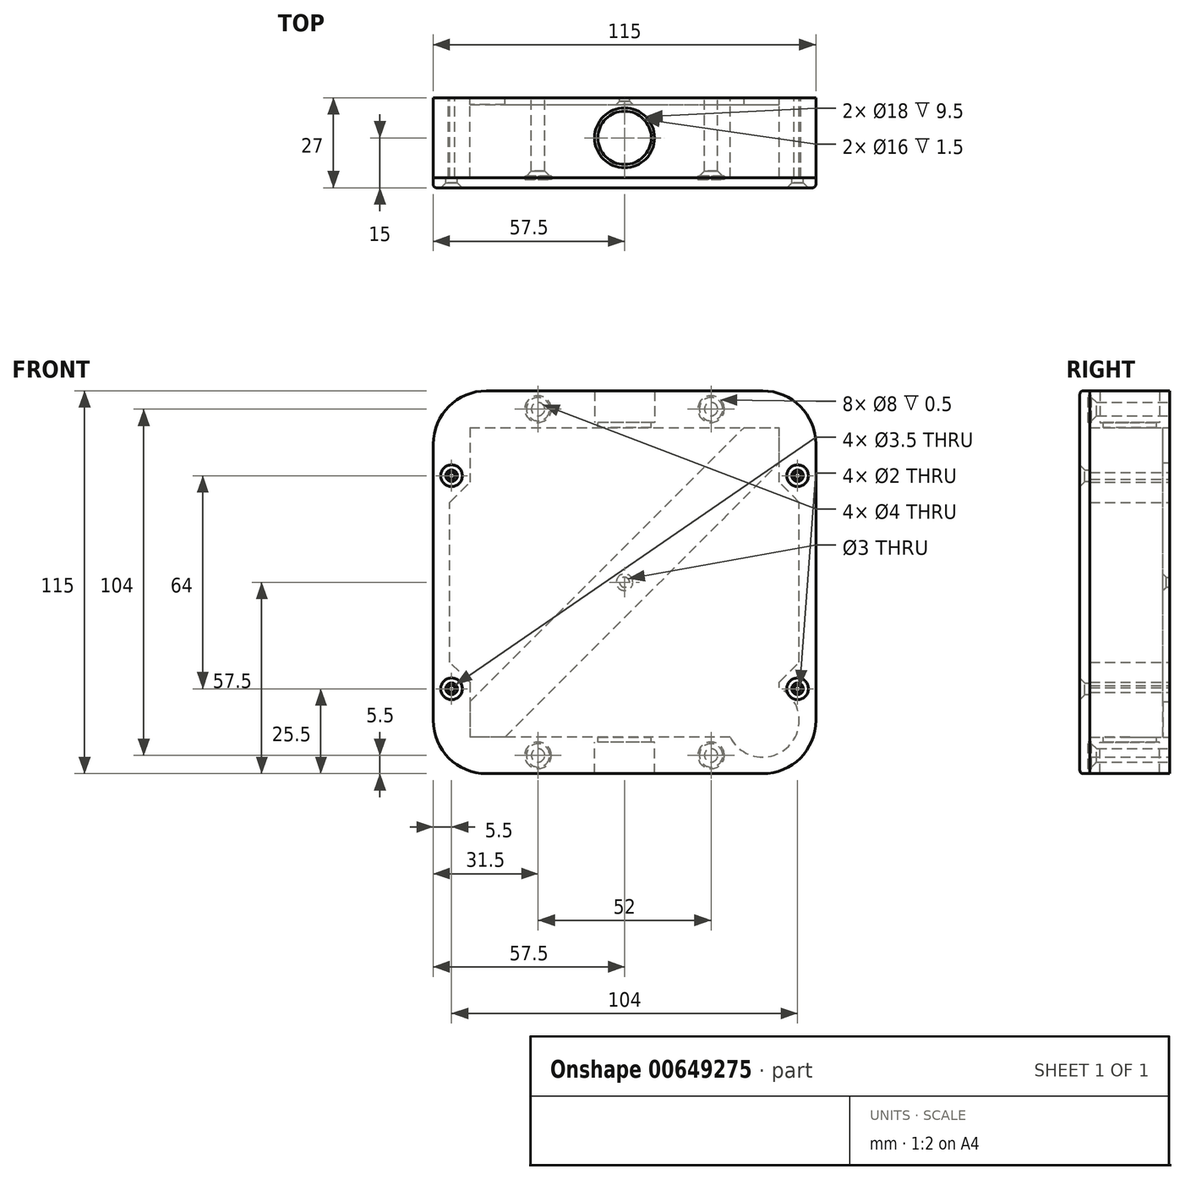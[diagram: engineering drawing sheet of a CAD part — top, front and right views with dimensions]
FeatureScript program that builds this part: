
annotation { "Feature Type Name" : "Feature", "Feature Type Description" : "" }
export const myFeature = defineFeature(function(context is Context, id is Id, definition is map)
    precondition{}
    {
        {
            var Q0;
            Q0=qCreatedBy(makeId("Front.planeOp"),FACE);
            var sketch = newSketch(context, id + "F0", { "sketchPlane" : qUnion([Q0])});
            skCircle(sketch, "E0", {"center": v(-26, 122) * mm, "radius": 2 * mm});
            skCircle(sketch, "E1", {"center": v(26, 18) * mm, "radius": 2 * mm});
            skLineSegment(sketch, "E2", {"start": v(46.5, 70) * mm, "end": v(-46.5, 70) * mm});
            skLineSegment(sketch, "E3.bottom", {"start": v(-46.5, 116.5) * mm, "end": v(46.5, 116.5) * mm});
            skLineSegment(sketch, "E3.left", {"start": v(-46.5, 116.5) * mm, "end": v(-46.5, 23.5) * mm});
            skArc(sketch, "E4", {"start": v(31.7, 23.5) * mm, "mid": v(49.28, 20.72) * mm, "end": v(46.5, 38.3) * mm});
            skArc(sketch, "E5", {"start": v(41.5, 12.5) * mm, "mid": v(52.81, 17.19) * mm, "end": v(57.5, 28.5) * mm});
            skArc(sketch, "E6", {"start": v(-57.5, 28.5) * mm, "mid": v(-52.81, 17.19) * mm, "end": v(-41.5, 12.5) * mm});
            skArc(sketch, "E7", {"start": v(-41.5, 127.5) * mm, "mid": v(-52.81, 122.81) * mm, "end": v(-57.5, 111.5) * mm});
            skArc(sketch, "E8", {"start": v(41.5, 127.5) * mm, "mid": v(52.81, 122.81) * mm, "end": v(57.5, 111.5) * mm});
            skLineSegment(sketch, "E9", {"start": v(0, 70) * mm, "end": v(0, 53.27) * mm});
            skLineSegment(sketch, "E10", {"start": v(-57.5, 28.5) * mm, "end": v(-57.5, 111.5) * mm});
            skLineSegment(sketch, "E11", {"start": v(-41.5, 127.5) * mm, "end": v(41.5, 127.5) * mm});
            skLineSegment(sketch, "E12", {"start": v(57.5, 111.5) * mm, "end": v(57.5, 28.5) * mm});
            skLineSegment(sketch, "E13", {"start": v(41.5, 12.5) * mm, "end": v(-41.5, 12.5) * mm});
            skCircle(sketch, "E14", {"center": v(-26, 18) * mm, "radius": 2 * mm});
            skCircle(sketch, "E15", {"center": v(26, 122) * mm, "radius": 2 * mm});
            skLineSegment(sketch, "E16", {"start": v(46.5, 38.3) * mm, "end": v(46.5, 116.5) * mm});
            skLineSegment(sketch, "E17", {"start": v(31.7, 23.5) * mm, "end": v(-46.5, 23.5) * mm});
            skCircle(sketch, "E18", {"center": v(52, 38) * mm, "radius": 1 * mm});
            skCircle(sketch, "E19", {"center": v(-52, 102) * mm, "radius": 1 * mm});
            skCircle(sketch, "E20", {"center": v(52, 102) * mm, "radius": 1 * mm});
            skCircle(sketch, "E21", {"center": v(-52, 38) * mm, "radius": 1 * mm});
            skLineSegment(sketch, "E22", {"start": v(-35.9, 23.5) * mm, "end": v(46.5, 105.9) * mm});
            skLineSegment(sketch, "E23", {"start": v(-46.5, 34.1) * mm, "end": v(35.9, 116.5) * mm});
            skCircle(sketch, "E24", {"center": v(0, 70) * mm, "radius": 1.5 * mm});
            skLineSegment(sketch, "E25", {"start": v(-46.5, 40) * mm, "end": v(-52.5, 46) * mm});
            skLineSegment(sketch, "E26", {"start": v(-52.5, 46) * mm, "end": v(-52.5, 94) * mm});
            skLineSegment(sketch, "E27", {"start": v(-52.5, 94) * mm, "end": v(-46.5, 100) * mm});
            skLineSegment(sketch, "E28", {"start": v(46.5, 40) * mm, "end": v(52.5, 46) * mm});
            skLineSegment(sketch, "E29", {"start": v(52.5, 46) * mm, "end": v(52.5, 94) * mm});
            skLineSegment(sketch, "E30", {"start": v(52.5, 94) * mm, "end": v(46.5, 100) * mm});
            skSolve(sketch);
        }
        {
            var Q0;
            Q0=qSketchRegion(id+"F0",true);
            extrude(context, id + "F1", {"entities" : qUnion([Q0]), "depth" : 24 * mm, "offsetDistance" : 25 * mm});
        }
        {
            var Q0;
            Q0=makeQuery(id+"F1.opExtrude","CAP_EDGE",EDGE,{"disambiguationData":[OSD([sQuery(id+"F0.wireOp",EDGE,"E0")])],"isStart":false});
            var Q1;
            Q1=makeQuery(id+"F1.opExtrude","CAP_EDGE",EDGE,{"disambiguationData":[OSD([sQuery(id+"F0.wireOp",EDGE,"E1")])],"isStart":false});
            var Q2;
            Q2=makeQuery(id+"F1.opExtrude","CAP_EDGE",EDGE,{"disambiguationData":[OSD([sQuery(id+"F0.wireOp",EDGE,"E14")])],"isStart":false});
            var Q3;
            Q3=makeQuery(id+"F1.opExtrude","CAP_EDGE",EDGE,{"disambiguationData":[OSD([sQuery(id+"F0.wireOp",EDGE,"E15")])],"isStart":false});
            chamfer(context, id + "F2", {"entities" : qUnion([Q0, Q1, Q2, Q3]), "width" : 2 * mm, "tangentPropagation" : true});
        }
        {
            var Q0;
            Q0=qCreatedBy(makeId("Top.planeOp"),FACE);
            cPlane(context, id + "F3", {"entities" : qUnion([Q0]), "cplaneType" : CPlaneType.OFFSET, "offset" : 118 * mm, "width" : 150 * mm, "height" : 150 * mm});
        }
        {
            var Q0;
            Q0=qCreatedBy(id+"F3.planeOp",FACE);
            var sketch = newSketch(context, id + "F4", { "sketchPlane" : qUnion([Q0])});
            skCircle(sketch, "E31", {"center": v(0, -12) * mm, "radius": 9 * mm});
            skCircle(sketch, "E32", {"center": v(0, -12) * mm, "radius": 8 * mm});
            skSolve(sketch);
        }
        {
            var Q0;
            Q0=qSketchRegion(id+"F4",true);
            extrude(context, id + "F5", {"entities" : qUnion([Q0]), "operationType" : NewBodyOperationType.REMOVE, "oppositeDirection" : true, "depth" : -25 * mm, "offsetDistance" : 25 * mm});
        }
        {
            var Q0;
            Q0=makeQuery(id+"F4.imprint","IMPRINT",FACE,{"disambiguationData":[TD([[makeQuery(id+"F4.imprint","IMPRINT",EDGE,{"derivedFrom":sQuery(id+"F4.wireOp",EDGE,"E32")}),1.0]])]});
            extrude(context, id + "F6", {"entities" : qUnion([Q0]), "operationType" : NewBodyOperationType.REMOVE, "endBound" : BoundingType.SYMMETRIC, "oppositeDirection" : true, "depth" : 27 * mm, "offsetDistance" : 25 * mm});
        }
        {
            var Q0;
            Q0=qCreatedBy(makeId("Top.planeOp"),FACE);
            cPlane(context, id + "F7", {"entities" : qUnion([Q0]), "cplaneType" : CPlaneType.OFFSET, "offset" : 22 * mm, "width" : 150 * mm, "height" : 150 * mm});
        }
        {
            var Q0;
            Q0=qCreatedBy(id+"F7.planeOp",FACE);
            var sketch = newSketch(context, id + "F8", { "sketchPlane" : qUnion([Q0])});
            skCircle(sketch, "E33", {"center": v(0, -12) * mm, "radius": 8 * mm});
            skCircle(sketch, "E34", {"center": v(0, -12) * mm, "radius": 9 * mm});
            skSolve(sketch);
        }
        {
            var Q0;
            Q0 = qSketchRegion(id + "F8", true);
            extrude(context, id + "F9", {"entities" : qUnion([Q0]), "operationType" : NewBodyOperationType.REMOVE, "oppositeDirection" : true, "depth" : 25 * mm, "offsetDistance" : 25 * mm});
        }
        {
            var Q0;
            Q0=makeQuery(id+"F8.imprint","IMPRINT",FACE,{"disambiguationData":[TD([[makeQuery(id+"F8.imprint","IMPRINT",EDGE,{"derivedFrom":sQuery(id+"F8.wireOp",EDGE,"E33")}),1.0]])]});
            extrude(context, id + "F10", {"entities" : qUnion([Q0]), "operationType" : NewBodyOperationType.REMOVE, "endBound" : BoundingType.SYMMETRIC, "oppositeDirection" : true, "depth" : 27 * mm, "offsetDistance" : 25 * mm});
        }
        {
            var Q0;
            Q0=qCreatedBy(makeId("Front.planeOp"),FACE);
            cPlane(context, id + "F11", {"entities" : qUnion([Q0]), "cplaneType" : CPlaneType.OFFSET, "offset" : 24 * mm, "width" : 150 * mm, "height" : 150 * mm});
        }
        {
            var Q0;
            Q0=qCreatedBy(id+"F11.planeOp",FACE);
            var sketch = newSketch(context, id + "F12", { "sketchPlane" : qUnion([Q0])});
            skArc(sketch, "E35", {"start": v(-41.5, 127.5) * mm, "mid": v(-52.81, 122.81) * mm, "end": v(-57.5, 111.5) * mm});
            skArc(sketch, "E36", {"start": v(57.5, 111.5) * mm, "mid": v(52.81, 122.81) * mm, "end": v(41.5, 127.5) * mm});
            skArc(sketch, "E37", {"start": v(57.5, 28.5) * mm, "mid": v(52.81, 17.19) * mm, "end": v(41.5, 12.5) * mm});
            skArc(sketch, "E38", {"start": v(-41.5, 12.5) * mm, "mid": v(-52.81, 17.19) * mm, "end": v(-57.5, 28.5) * mm});
            skLineSegment(sketch, "E39", {"start": v(-41.5, 127.5) * mm, "end": v(41.5, 127.5) * mm});
            skLineSegment(sketch, "E40", {"start": v(57.5, 111.5) * mm, "end": v(57.5, 28.5) * mm});
            skLineSegment(sketch, "E41", {"start": v(41.5, 12.5) * mm, "end": v(-41.5, 12.5) * mm});
            skLineSegment(sketch, "E42", {"start": v(-57.5, 28.5) * mm, "end": v(-57.5, 111.5) * mm});
            skCircle(sketch, "E43", {"center": v(52, 38) * mm, "radius": 1.75 * mm});
            skCircle(sketch, "E44", {"center": v(52, 102) * mm, "radius": 1.75 * mm});
            skCircle(sketch, "E45", {"center": v(-52, 102) * mm, "radius": 1.75 * mm});
            skCircle(sketch, "E46", {"center": v(-52, 38) * mm, "radius": 1.75 * mm});
            skCircle(sketch, "E47", {"center": v(-26, 122) * mm, "radius": 4 * mm});
            skCircle(sketch, "E48", {"center": v(26, 122) * mm, "radius": 4 * mm});
            skCircle(sketch, "E49", {"center": v(26, 18) * mm, "radius": 4 * mm});
            skCircle(sketch, "E50", {"center": v(-26, 18) * mm, "radius": 4 * mm});
            skSolve(sketch);
        }
        {
            var Q0;
            Q0 = qSketchRegion(id + "F12", true);
            var Q1;
            Q1=makeQuery(id+"F12.imprint","IMPRINT",FACE,{"disambiguationData":[TD([[makeQuery(id+"F12.imprint","IMPRINT",EDGE,{"derivedFrom":sQuery(id+"F12.wireOp",EDGE,"E35")}),1.0]])]});
            var Q2;
            Q2=makeQuery(id+"F12.imprint","IMPRINT",FACE,{"disambiguationData":[TD([[makeQuery(id+"F12.imprint","IMPRINT",EDGE,{"derivedFrom":sQuery(id+"F12.wireOp",EDGE,"E47")}),1.0]])]});
            var Q3;
            Q3=makeQuery(id+"F12.imprint","IMPRINT",FACE,{"disambiguationData":[TD([[makeQuery(id+"F12.imprint","IMPRINT",EDGE,{"derivedFrom":sQuery(id+"F12.wireOp",EDGE,"E48")}),1.0]])]});
            var Q4;
            Q4=makeQuery(id+"F12.imprint","IMPRINT",FACE,{"disambiguationData":[TD([[makeQuery(id+"F12.imprint","IMPRINT",EDGE,{"derivedFrom":sQuery(id+"F12.wireOp",EDGE,"E50")}),1.0]])]});
            var Q5;
            Q5=makeQuery(id+"F12.imprint","IMPRINT",FACE,{"disambiguationData":[TD([[makeQuery(id+"F12.imprint","IMPRINT",EDGE,{"derivedFrom":sQuery(id+"F12.wireOp",EDGE,"E49")}),1.0]])]});
            extrude(context, id + "F13", {"entities" : qUnion([Q0, Q1, Q2, Q3, Q4, Q5]), "depth" : 3 * mm, "offsetDistance" : 25 * mm});
        }
        {
            var Q0;
            Q0=makeQuery(id+"F13.opExtrude","CAP_EDGE",EDGE,{"disambiguationData":[OSD([sQuery(id+"F12.wireOp",EDGE,"E45")])],"isStart":false});
            var Q1;
            Q1=makeQuery(id+"F13.opExtrude","CAP_EDGE",EDGE,{"disambiguationData":[OSD([sQuery(id+"F12.wireOp",EDGE,"E46")])],"isStart":false});
            var Q2;
            Q2=makeQuery(id+"F13.opExtrude","CAP_EDGE",EDGE,{"disambiguationData":[OSD([sQuery(id+"F12.wireOp",EDGE,"E43")])],"isStart":false});
            var Q3;
            Q3=makeQuery(id+"F13.opExtrude","CAP_EDGE",EDGE,{"disambiguationData":[OSD([sQuery(id+"F12.wireOp",EDGE,"E44")])],"isStart":false});
            chamfer(context, id + "F14", {"entities" : qUnion([Q0, Q1, Q2, Q3]), "width" : 1.5 * mm, "tangentPropagation" : true});
        }
        {
            var Q0;
            Q0=makeQuery(id+"F13.opExtrude","CAP_EDGE",EDGE,{"disambiguationData":[OSD([sQuery(id+"F12.wireOp",EDGE,"E42")])],"isStart":false});
            fillet(context, id + "F15", {"entities" : qUnion([Q0]), "radius" : 1 * mm, "tangentPropagation" : true, "allowEdgeOverflow" : false});
        }
        {
            var Q0;
            Q0=makeQuery(id+"F12.imprint","IMPRINT",FACE,{"disambiguationData":[TD([[makeQuery(id+"F12.imprint","IMPRINT",EDGE,{"derivedFrom":sQuery(id+"F12.wireOp",EDGE,"E47")}),1.0]])]});
            var Q1;
            Q1=makeQuery(id+"F12.imprint","IMPRINT",FACE,{"disambiguationData":[TD([[makeQuery(id+"F12.imprint","IMPRINT",EDGE,{"derivedFrom":sQuery(id+"F12.wireOp",EDGE,"E48")}),1.0]])]});
            var Q2;
            Q2=makeQuery(id+"F12.imprint","IMPRINT",FACE,{"disambiguationData":[TD([[makeQuery(id+"F12.imprint","IMPRINT",EDGE,{"derivedFrom":sQuery(id+"F12.wireOp",EDGE,"E50")}),1.0]])]});
            var Q3;
            Q3=makeQuery(id+"F12.imprint","IMPRINT",FACE,{"disambiguationData":[TD([[makeQuery(id+"F12.imprint","IMPRINT",EDGE,{"derivedFrom":sQuery(id+"F12.wireOp",EDGE,"E49")}),1.0]])]});
            extrude(context, id + "F16", {"entities" : qUnion([Q0, Q1, Q2, Q3]), "operationType" : NewBodyOperationType.REMOVE, "endBound" : BoundingType.SYMMETRIC, "oppositeDirection" : true, "depth" : 1 * mm, "offsetDistance" : 25 * mm});
        }
        {
            var Q0;
            Q0 = qSketchRegion(id + "F0", true);
            var Q1;
            {var subQ7=sQuery(id+"F0.wireOp",EDGE,"E24");var subQ9=sQuery(id+"F0.wireOp",EDGE,"E2");var subQ10=makeQuery(id+"F0.imprint","INTERSECT",VERTEX,{"disambiguationData":[OD(1.0)],"derivedFrom":[subQ9,subQ7]});Q1=makeQuery(id+"F0.imprint","IMPRINT",FACE,{"disambiguationData":[TD([[makeQuery(id+"F0.imprint","IMPRINT",EDGE,{"disambiguationData":[TD([[subQ10,-1.0]])],"derivedFrom":subQ9}),1.0]])]});}
            var Q2;
            {var subQ0=sQuery(id+"F0.wireOp",EDGE,"E22");var subQ1=sQuery(id+"F0.wireOp",EDGE,"E2");var subQ2=makeQuery(id+"F0.imprint","INTERSECT",VERTEX,{"derivedFrom":[subQ1,subQ0]});Q2=makeQuery(id+"F0.imprint","IMPRINT",FACE,{"disambiguationData":[TD([[makeQuery(id+"F0.imprint","IMPRINT",EDGE,{"disambiguationData":[TD([[subQ2,-1.0]])],"derivedFrom":subQ1}),1.0]])]});}
            var Q3;
            {var subQ6=sQuery(id+"F0.wireOp",EDGE,"E2");var subQ9=sQuery(id+"F0.wireOp",EDGE,"E22");var subQ11=makeQuery(id+"F0.imprint","INTERSECT",VERTEX,{"derivedFrom":[subQ6,subQ9]});Q3=makeQuery(id+"F0.imprint","IMPRINT",FACE,{"disambiguationData":[TD([[makeQuery(id+"F0.imprint","IMPRINT",EDGE,{"disambiguationData":[TD([[subQ11,-1.0]])],"derivedFrom":subQ6}),-1.0]])]});}
            extrude(context, id + "F17", {"entities" : qUnion([Q0, Q1, Q2, Q3]), "operationType" : NewBodyOperationType.ADD, "depth" : 2 * mm, "offsetDistance" : 25 * mm});
        }
        {
            var Q0;
            Q0=makeQuery(id+"F17.opExtrude","CAP_EDGE",EDGE,{"disambiguationData":[OSD([sQuery(id+"F0.wireOp",EDGE,"E24")])],"isStart":false});
            chamfer(context, id + "F18", {"entities" : qUnion([Q0]), "width" : 1 * mm, "tangentPropagation" : true});
        }
    });
